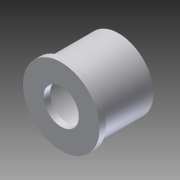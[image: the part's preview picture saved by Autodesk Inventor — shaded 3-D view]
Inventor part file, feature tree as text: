
AUTODESK INVENTOR PART (.ipt)
format: ipt  version: 2014 SP1 (Build 180222100, 222)  size: 100,352 bytes
history: native  units: in
note: dims shown in document units (in); Inventor stores cm internally (conversion verified against a paired STEP export)
features: extrude x3, sketch x2
ambient origin geometry x8: Origin, YZ Plane, XZ Plane, XY Plane, X Axis, Y Axis, Z Axis, Center Point
bodies: Solid1 (feature_tree)
feature tree (5):
  sketch  "Sketch1"  dims[d0=1.36in d1=1.5in]
  extrude  "Extrusion1"  Depth=1.5in
  extrude  "Extrusion2"  Depth=1.0in TaperAngle=0.0deg
  extrude  "Extrusion3"  Depth=1.0in
  sketch  "Sketch2"  dims[d2=0.125in d3=0.0in d4=1.0in d5=0.0in d6=1.25in d7=0.6875in d8=1.0in d9=0.0in]
